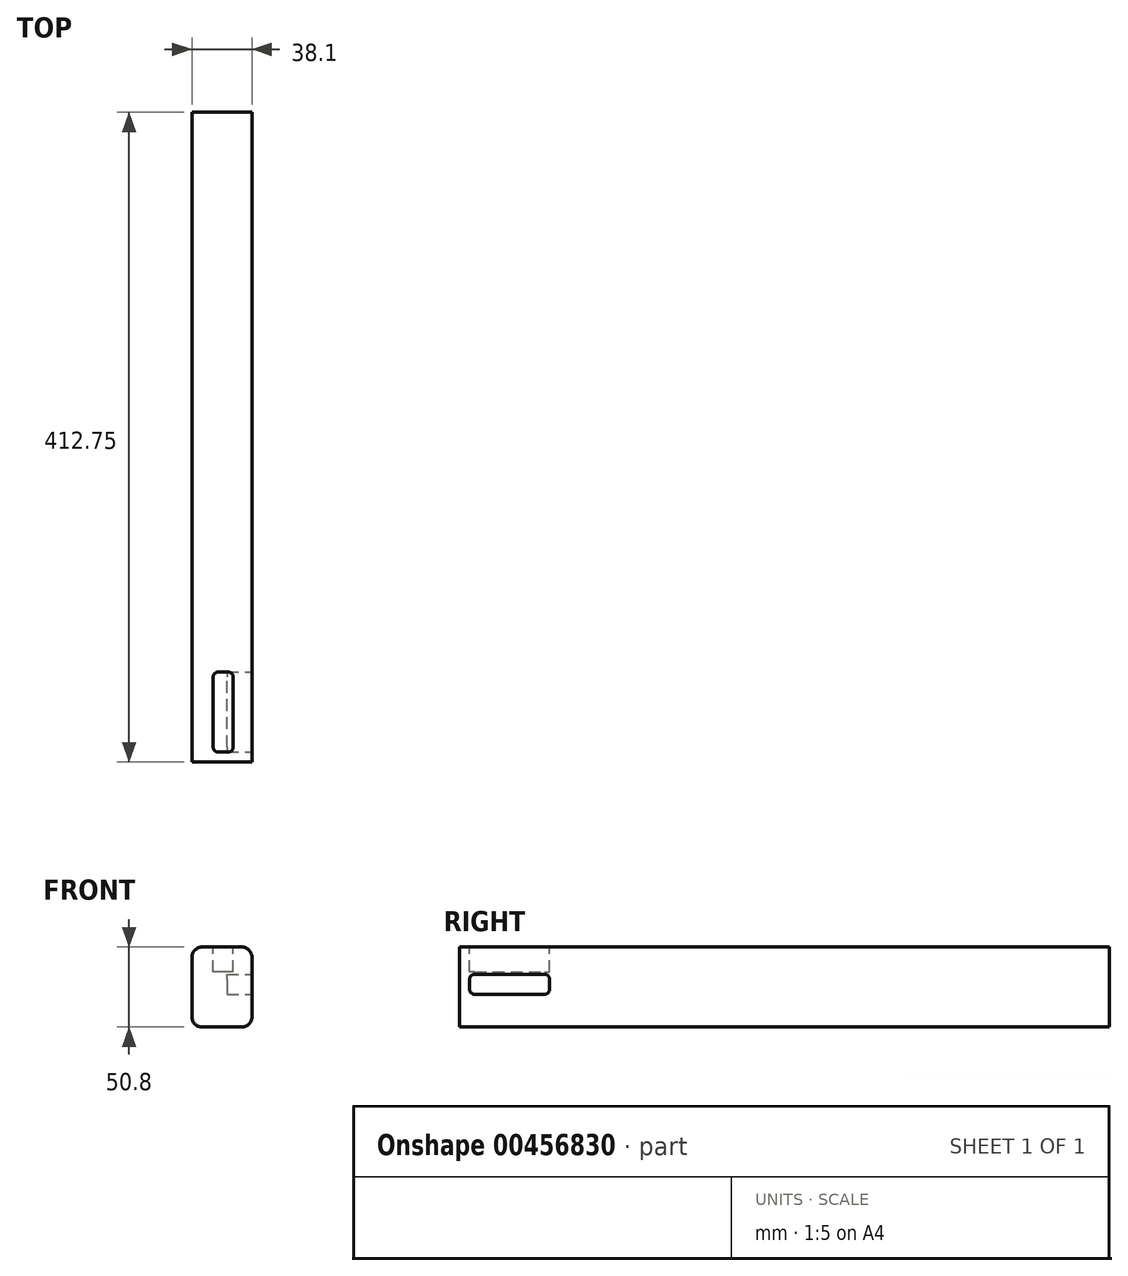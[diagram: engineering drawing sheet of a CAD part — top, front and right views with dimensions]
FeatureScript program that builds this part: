
annotation { "Feature Type Name" : "Feature", "Feature Type Description" : "" }
export const myFeature = defineFeature(function(context is Context, id is Id, definition is map)
    precondition{}
    {
        {
            var Q0;
            Q0=qCreatedBy(makeId("Front.planeOp"),FACE);
            var sketch = newSketch(context, id + "F0", { "sketchPlane" : qUnion([Q0])});
            skLineSegment(sketch, "E0", {"start": v(-21.46, 29.96) * mm, "end": v(16.64, 29.96) * mm});
            skLineSegment(sketch, "E1", {"start": v(16.64, 29.96) * mm, "end": v(16.64, -20.84) * mm});
            skLineSegment(sketch, "E2", {"start": v(16.64, -20.84) * mm, "end": v(-21.46, -20.84) * mm});
            skLineSegment(sketch, "E3", {"start": v(-21.46, -20.84) * mm, "end": v(-21.46, 29.96) * mm});
            skSolve(sketch);
        }
        {
            var Q0;
            Q0 = qSketchRegion(id + "F0", true);
            extrude(context, id + "F1", {"entities" : qUnion([Q0]), "oppositeDirection" : true, "depth" : 412.75 * mm});
        }
        {
            var Q0;
            Q0=makeQuery(id+"F1.opExtrude","SWEPT_FACE",FACE,{"disambiguationData":[OSD([sQuery(id+"F0.wireOp",EDGE,"E1")])]});
            var sketch = newSketch(context, id + "F2", { "sketchPlane" : qUnion([Q0])});
            skLineSegment(sketch, "E4", {"start": v(9.52, 12.7) * mm, "end": v(53.98, 12.7) * mm});
            skLineSegment(sketch, "E5", {"start": v(57.15, 9.53) * mm, "end": v(57.15, 3.18) * mm});
            skLineSegment(sketch, "E6", {"start": v(53.98, 0) * mm, "end": v(9.52, 0) * mm});
            skLineSegment(sketch, "E7", {"start": v(6.35, 3.18) * mm, "end": v(6.35, 9.52) * mm});
            skPoint(sketch, "E8.visualSharp", {"position": v(57.15, 12.7) * mm});
            skArc(sketch, "E8.filletArc", {"start": v(57.15, 9.53) * mm, "mid": v(56.22, 11.77) * mm, "end": v(53.98, 12.7) * mm});
            skPoint(sketch, "E9.visualSharp", {"position": v(57.15, 0) * mm});
            skArc(sketch, "E9.filletArc", {"start": v(53.98, 0) * mm, "mid": v(56.22, 0.93) * mm, "end": v(57.15, 3.18) * mm});
            skPoint(sketch, "E10.visualSharp", {"position": v(6.35, 12.7) * mm});
            skArc(sketch, "E10.filletArc", {"start": v(9.52, 12.7) * mm, "mid": v(7.28, 11.77) * mm, "end": v(6.35, 9.52) * mm});
            skPoint(sketch, "E11.visualSharp", {"position": v(6.35, 0) * mm});
            skArc(sketch, "E11.filletArc", {"start": v(6.35, 3.18) * mm, "mid": v(7.28, 0.93) * mm, "end": v(9.52, 0) * mm});
            skSolve(sketch);
        }
        {
            var Q0;
            Q0 = qSketchRegion(id + "F2", true);
            extrude(context, id + "F3", {"entities" : qUnion([Q0]), "operationType" : NewBodyOperationType.REMOVE, "oppositeDirection" : true, "depth" : 15.88 * mm});
        }
        {
            var Q0;
            Q0=makeQuery(id+"F1.opExtrude","SWEPT_FACE",FACE,{"disambiguationData":[OSD([sQuery(id+"F0.wireOp",EDGE,"E0")])]});
            var sketch = newSketch(context, id + "F4", { "sketchPlane" : qUnion([Q0])});
            skLineSegment(sketch, "E12", {"start": v(-7.97, 53.98) * mm, "end": v(-7.97, 9.52) * mm});
            skLineSegment(sketch, "E13", {"start": v(-4.8, 6.35) * mm, "end": v(1.55, 6.35) * mm});
            skLineSegment(sketch, "E14", {"start": v(4.73, 9.53) * mm, "end": v(4.73, 53.98) * mm});
            skLineSegment(sketch, "E15", {"start": v(1.55, 57.15) * mm, "end": v(-4.8, 57.15) * mm});
            skPoint(sketch, "E16.visualSharp", {"position": v(-7.97, 57.15) * mm});
            skArc(sketch, "E16.filletArc", {"start": v(-4.8, 57.15) * mm, "mid": v(-7.04, 56.22) * mm, "end": v(-7.97, 53.98) * mm});
            skPoint(sketch, "E17.visualSharp", {"position": v(4.73, 57.15) * mm});
            skArc(sketch, "E17.filletArc", {"start": v(4.73, 53.98) * mm, "mid": v(3.8, 56.22) * mm, "end": v(1.55, 57.15) * mm});
            skPoint(sketch, "E18.visualSharp", {"position": v(4.73, 6.35) * mm});
            skArc(sketch, "E18.filletArc", {"start": v(1.55, 6.35) * mm, "mid": v(3.8, 7.28) * mm, "end": v(4.73, 9.53) * mm});
            skPoint(sketch, "E19.visualSharp", {"position": v(-7.97, 6.35) * mm});
            skArc(sketch, "E19.filletArc", {"start": v(-7.97, 9.52) * mm, "mid": v(-7.04, 7.28) * mm, "end": v(-4.8, 6.35) * mm});
            skSolve(sketch);
        }
        {
            var Q0;
            Q0 = qSketchRegion(id + "F4", true);
            extrude(context, id + "F5", {"entities" : qUnion([Q0]), "operationType" : NewBodyOperationType.REMOVE, "oppositeDirection" : true, "depth" : 15.88 * mm});
        }
        {
            var Q0;
            Q0=makeQuery(id+"F1.opExtrude","SWEPT_EDGE",EDGE,{"disambiguationData":[OSD([sQuery(id+"F0.wireOp",EDGE,"E1"),sQuery(id+"F0.wireOp",EDGE,"E2")])]});
            var Q1;
            Q1=makeQuery(id+"F1.opExtrude","SWEPT_EDGE",EDGE,{"disambiguationData":[OSD([sQuery(id+"F0.wireOp",EDGE,"E2"),sQuery(id+"F0.wireOp",EDGE,"E3")])]});
            var Q2;
            Q2=makeQuery(id+"F1.opExtrude","SWEPT_EDGE",EDGE,{"disambiguationData":[OSD([sQuery(id+"F0.wireOp",EDGE,"E0"),sQuery(id+"F0.wireOp",EDGE,"E1")])]});
            var Q3;
            Q3=makeQuery(id+"F1.opExtrude","SWEPT_EDGE",EDGE,{"disambiguationData":[OSD([sQuery(id+"F0.wireOp",EDGE,"E0"),sQuery(id+"F0.wireOp",EDGE,"E3")])]});
            fillet(context, id + "F6", {"entities" : qUnion([Q0, Q1, Q2, Q3]), "radius" : 6.35 * mm, "tangentPropagation" : true, "allowEdgeOverflow" : false});
        }
    });
